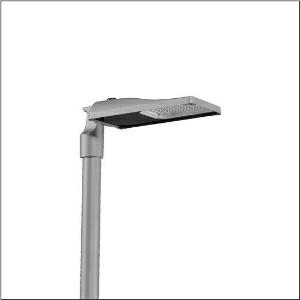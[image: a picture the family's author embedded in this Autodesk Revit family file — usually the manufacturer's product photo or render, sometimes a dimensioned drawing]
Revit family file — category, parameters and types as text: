
# Revit family: streetlight_sl_31_mini___st1_0a_5xh2d3as08ga_13ac
name_source: partatom
category: Lighting Fixtures
units: mm (PartAtom-declared; Revit-internal decimal feet)

## family parameters
Cut with Voids When Loaded = No
Host = Face
Light Source = No
Part Type = Normal
Room Calculation Point = No
Round Connector Dimension = Use Diameter
Shared = No

## types (1)
- --- (1 x LED, 5880 lm, 39.3 W, 3000K)
    Apparent Load = 39 VA
    CIE Flux Codes = 37 72 97 100 100
    Color Rendering = 70
    Color Temperature = 3000K
    Default Elevation = 1800 mm
    Description = Streetlight SL 31 mini D4i mast luminaire for post-top, side-entry; light control with lens of PMMA; light distribution: ST1.0a, direct asymmetric distribution, for standard-compliant lighting for roads and squares; LED: luminous flux: 5.880lm, light colour: 730, colour temperature: 3000K; luminous efficacy: 149,6lm/W; control: pre-setting: logarithmic dimming characteristic, flexible luminous flux parameterisation, time-dependent luminous flux control, constant luminous flux control, power reduction, intelligent temperature release in ECG and LED module, overheat protection; luminaire housing, of diecast aluminium, Siteco® metallic grey (DB 702S), corrosivity category C5 high according to DIN EN ISO 12944; cover of toughened safety glass, transparent, mast flange of diecast aluminium, Siteco® metallic grey (DB 702S), spigot size: 76/60mm, mast flange included unmounted; with cable H07RN-F 2x 1.5mm², cable length: 8,5m, connection cable pre-assembled; mains connection: 220..240V, AC, 50/60Hz; power consumption (at start of service life): 39,3W / (at end of service life): 40,7W / (with reduced operation 50%): 18,1W; protection rating (complete): IP66; insulation class (complete): insulation class II (safety insulation); impact resistance: IK10; certification: CE, ENEC, ENEC+, VDE, UKCA, ZD4i; permissible operating ambient temperature for outdoor applications: -40..+50°C; packaging unit: 1 piece

Light Distribution: ST1.0a
    Height = 76 mm
    Lamp = 1 x LED
    Lamp Light Flux = 5880 lm
    Lamp Power = 39.3 W
    Lamp count = 1
    Length = 547 mm
    Luminous efficacy = 150 lm/W
    Manufacturer = Siteco
    ModVariant = No
    Model = 5XH2D3AS08GA
    Number of Poles = 1
    OnlyDefault = Yes
    Power Factor = 1
    Product Name = Streetlight SL 31 mini | ST1.0a
    Product group = mast luminaire | pylon top
    ProductGroupID = 6100
    Protection Class = Protection class II
    Protection Degree = IP 66
    RLX_Detail_Level = 1
    RLX_Emergency_Light_Flux = 0 lm
    RLX_Emergency_Type = 0
    RLX_Emergency_Type_DB = No
    RlxData = <blob elided: 39697 chars, md5=35ce2f62>
    Socket = socket
    Standby Power = 0 W
    System Light Flux = 5880 lm
    System Power = 39 W
    Type Comments = factory setting: luminous flux: 100 % | dim-lin: 254 | 798 mA
    Type Image = l_1300330.jpg
    URL = http://relux.com
    VarID = @adj_054784
    Voltage = 0 V
    Weight = 0.00 kg
    Width = 265 mm

## geometry (parser evidence)
native form markers: Blend x4, Sweep x8
no freeform markers — native parametric forms only
